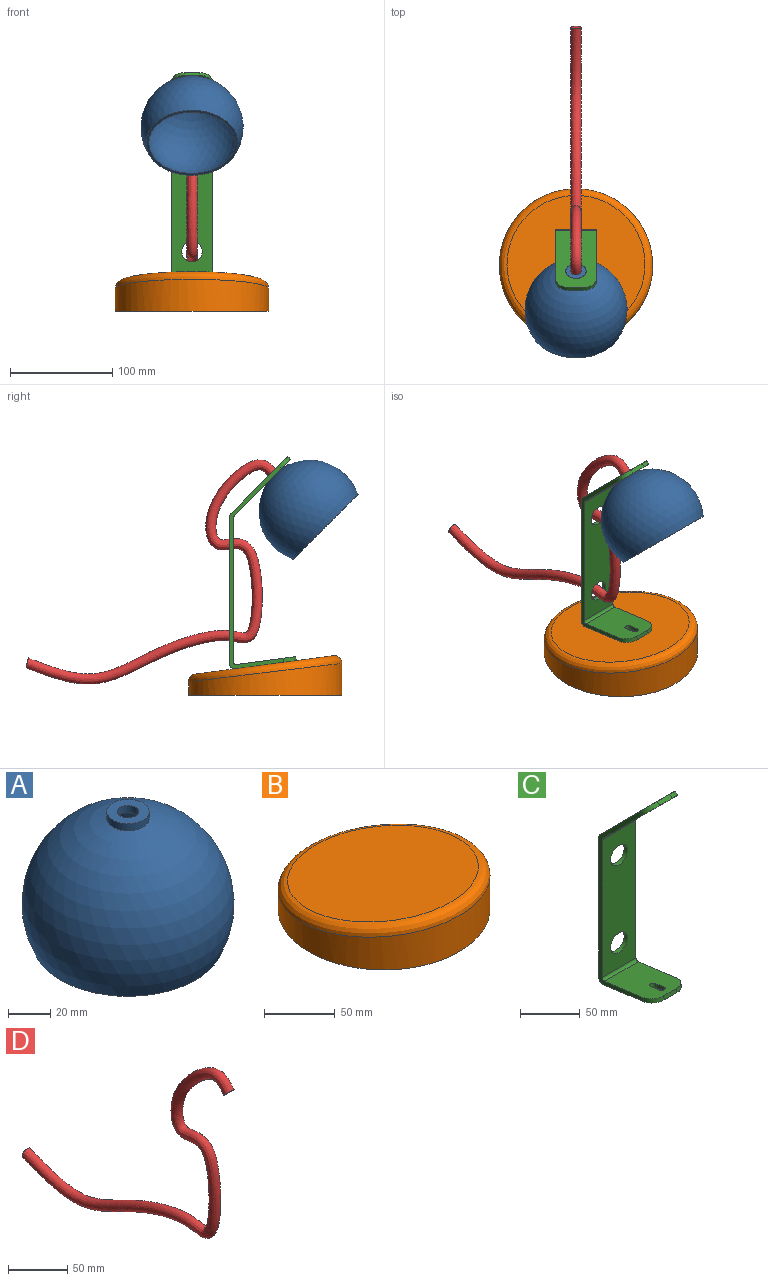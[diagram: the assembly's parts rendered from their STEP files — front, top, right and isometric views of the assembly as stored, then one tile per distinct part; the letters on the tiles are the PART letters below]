
ASSEMBLY  parts=4 mates=3
PART A: 8 faces, bbox 100x100x74.8 mm
  f0: cylinder r=10mm len=20mm, axis (0,0,1), area 251.3mm2, adj f1,f4
  f1: sphere r=50mm, area 22237.5mm2, adj f0,f2
  f2: plane 90x90mm, normal (0,0,-1), area 765.8mm2, adj f1,f7
  f3: cylinder r=5mm len=10mm, axis (0,0,1), area 125.7mm2, adj f4,f5
  f4: plane 20x20mm, normal (0,0,1), area 235.6mm2, adj f0,f3
  f5: plane 15x15mm, normal (0,0,-1), area 98.2mm2, adj f3,f6
  f6: cylinder r=7.5mm len=15mm, axis (0,0,1), area 98.3mm2, adj f5,f7
  f7: sphere r=47.5mm, area 20503.2mm2, adj f2,f6
PART B: 4 faces, bbox 150x150x38.9 mm
  f0: cylinder r=75mm len=150mm, axis (0,0,-1), area 10571.5mm2, adj f1,f3
  f1: plane 150x150mm, normal (0,0,-1), area 17671.5mm2, adj f0
  f2: plane 135x135mm, normal (0,0.13,0.99), area 14440.6mm2, adj f3
  f3: bspline ~149.92x149.85mm, area 5371.2mm2, adj f0,f2
PART C: 25 faces, bbox 40x65.1x207.7 mm
  f0: plane 143.77x40mm, normal (0,1,0), area 5122.5mm2, adj f3,f4,f12,f13,f18,f19
  f1: plane 141.44x40mm, normal (0,-1,0), area 5029.1mm2, adj f8,f9,f12,f13,f18,f19
  f2: plane 59.47x40mm, normal (0,-0.13,-0.99), area 2244.7mm2, adj f3,f11,f12,f13,f15,f17,f21,f22
  f3: cylinder r=5mm len=40mm, axis (-1,0,0), area 340.7mm2, adj f0,f2,f12,f13
  f4: cylinder r=5mm len=40mm, axis (-1,0,0), area 157.1mm2, adj f0,f5,f12,f13
  f5: plane 55.39x55.39mm, normal (0,0.71,0.71), area 2752.4mm2, adj f4,f6,f12,f13,f14,f16,f20
  f6: plane 15x2.83mm, normal (0,-0.71,0.71), area 60mm2, adj f5,f7,f14,f16
  f7: plane 54.96x54.96mm, normal (0,-0.71,-0.71), area 2727.5mm2, adj f6,f8,f12,f13,f14,f16,f20
  f8: cylinder r=2.5mm len=40mm, axis (-1,0,0), area 78.5mm2, adj f1,f7,f12,f13
  f9: cylinder r=2.5mm len=40mm, axis (-1,0,0), area 170.3mm2, adj f1,f10,f12,f13
  f10: plane 57.78x40mm, normal (0,0.13,0.99), area 2176.1mm2, adj f9,f11,f12,f13,f15,f17,f21,f22
  f11: plane 15x3.97mm, normal (0,-0.99,0.13), area 60mm2, adj f2,f10,f15,f17
  f12: plane 198.86x52.74mm, normal (1,0,0), area 1059.9mm2, adj f0,f1,f2,f3,f4,f5,f7,f8
  f13: plane 198.86x52.74mm, normal (-1,0,0), area 1059.9mm2, adj f0,f1,f2,f3,f4,f5,f7,f8
  f14: cylinder r=12.5mm len=12.5mm, axis (0,-0.71,-0.71), area 78.5mm2, adj f5,f6,f7,f13
  f15: cylinder r=12.5mm len=12.92mm, axis (0,-0.13,-0.99), area 78.5mm2, adj f2,f10,f11,f13
  f16: cylinder r=12.5mm len=12.5mm, axis (0,0.71,0.71), area 78.5mm2, adj f5,f6,f7,f12
  f17: cylinder r=12.5mm len=12.92mm, axis (0,0.13,0.99), area 78.5mm2, adj f2,f10,f11,f12
  f18: cylinder r=10mm len=20mm, axis (0,-1,0), area 251.3mm2, adj f0,f1
  f19: cylinder r=10mm len=20mm, axis (0,-1,0), area 251.3mm2, adj f0,f1
  f20: cylinder r=10mm len=20mm, axis (0,0.71,0.71), area 251.3mm2, adj f5,f7
  f21: plane 10.44x5.29mm, normal (1,0,0), area 40mm2, adj f2,f10,f22,f24
  f22: cylinder r=3mm len=6mm, axis (0,0.13,0.99), area 37.7mm2, adj f2,f10,f21,f23
  f23: plane 10.44x5.29mm, normal (-1,0,0), area 40mm2, adj f2,f10,f22,f24
  f24: cylinder r=3mm len=6mm, axis (0,0.13,0.99), area 37.7mm2, adj f2,f10,f21,f23
PART D: 3 faces, bbox 20x246.4x220.4 mm
  f0: plane 10x7.07mm, normal (0,-0.71,-0.71), area 78.5mm2, adj f2
  f1: plane 10x9.73mm, normal (0,0.97,0.23), area 78.5mm2, adj f2
  f2: bspline ~246.43x220.42mm, area 14598.4mm2, adj f0,f1
PLACE A rot(axis=(-1,0,0),45deg) t=(0,-58.83,164.95)mm
PLACE B at identity fixed
PLACE C t=(0,-0.4,0.05)mm
PLACE D t=(0,-0.4,0.05)mm
MATE fastened B.f2 <-> C.f2  axis (0,0.13,0.99) through (0,0.99,29.87)mm
MATE fastened A.f0 <-> C.f20  axis (0,0.71,0.71) through (0,-5.95,217.83)mm
MATE fastened D.f0 <-> C.f20  axis (0,-0.71,-0.71) through (0,-8.78,215.01)mm
